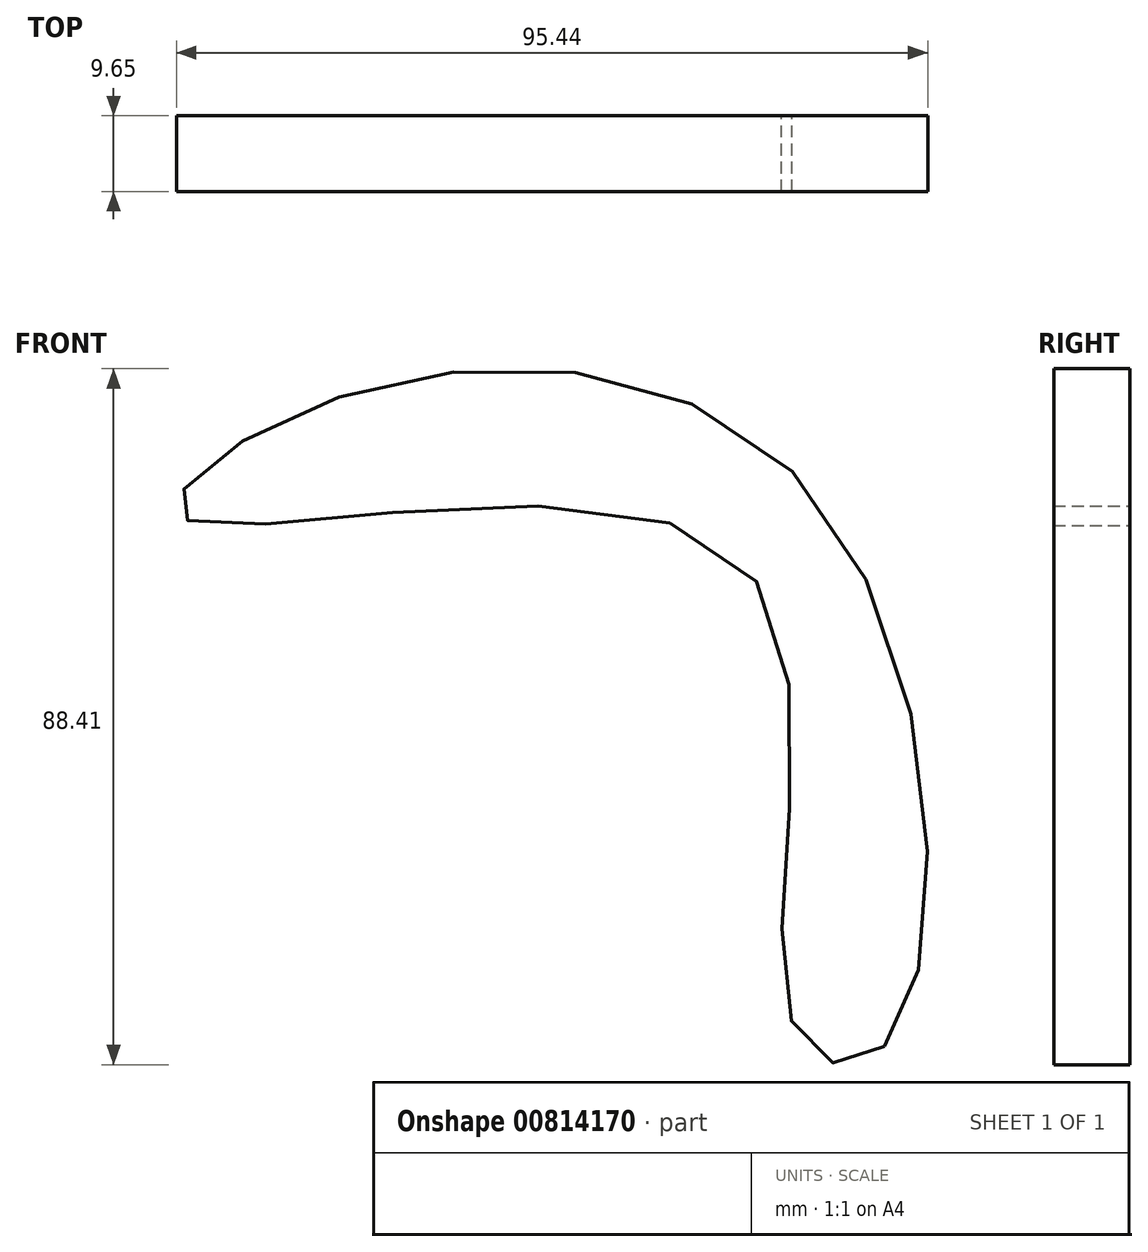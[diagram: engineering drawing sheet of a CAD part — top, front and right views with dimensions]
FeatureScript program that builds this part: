
annotation { "Feature Type Name" : "Feature", "Feature Type Description" : "" }
export const myFeature = defineFeature(function(context is Context, id is Id, definition is map)
    precondition{}
    {
        {
            var Q0;
            Q0=qCreatedBy(makeId("Front.planeOp"),FACE);
            var sketch = newSketch(context, id + "F0", { "sketchPlane" : qUnion([Q0])});
            skFitSpline(sketch, "E0", {"points": [v(-36.04, -32.76) * mm, v(-45.22, 37.46) * mm, v(-110.12, 47.95) * mm, v(-125.03, 34.21) * mm, v(-55.37, 29.68) * mm, v(-47.81, -29.79) * mm, v(-36.04, -32.76) * mm]});
            skSolve(sketch);
        }
        {
            var Q0;
            Q0=makeQuery(id+"F0.imprint","IMPRINT",FACE,{"disambiguationData":[TD([[makeQuery(id+"F0.imprint","IMPRINT",EDGE,{"derivedFrom":sQuery(id+"F0.wireOp",EDGE,"E0")}),1.0]])]});
            extrude(context, id + "F1", {"entities" : qUnion([Q0]), "depth" : 9.65 * mm, "offsetDistance" : 25.4 * mm});
        }
    });
